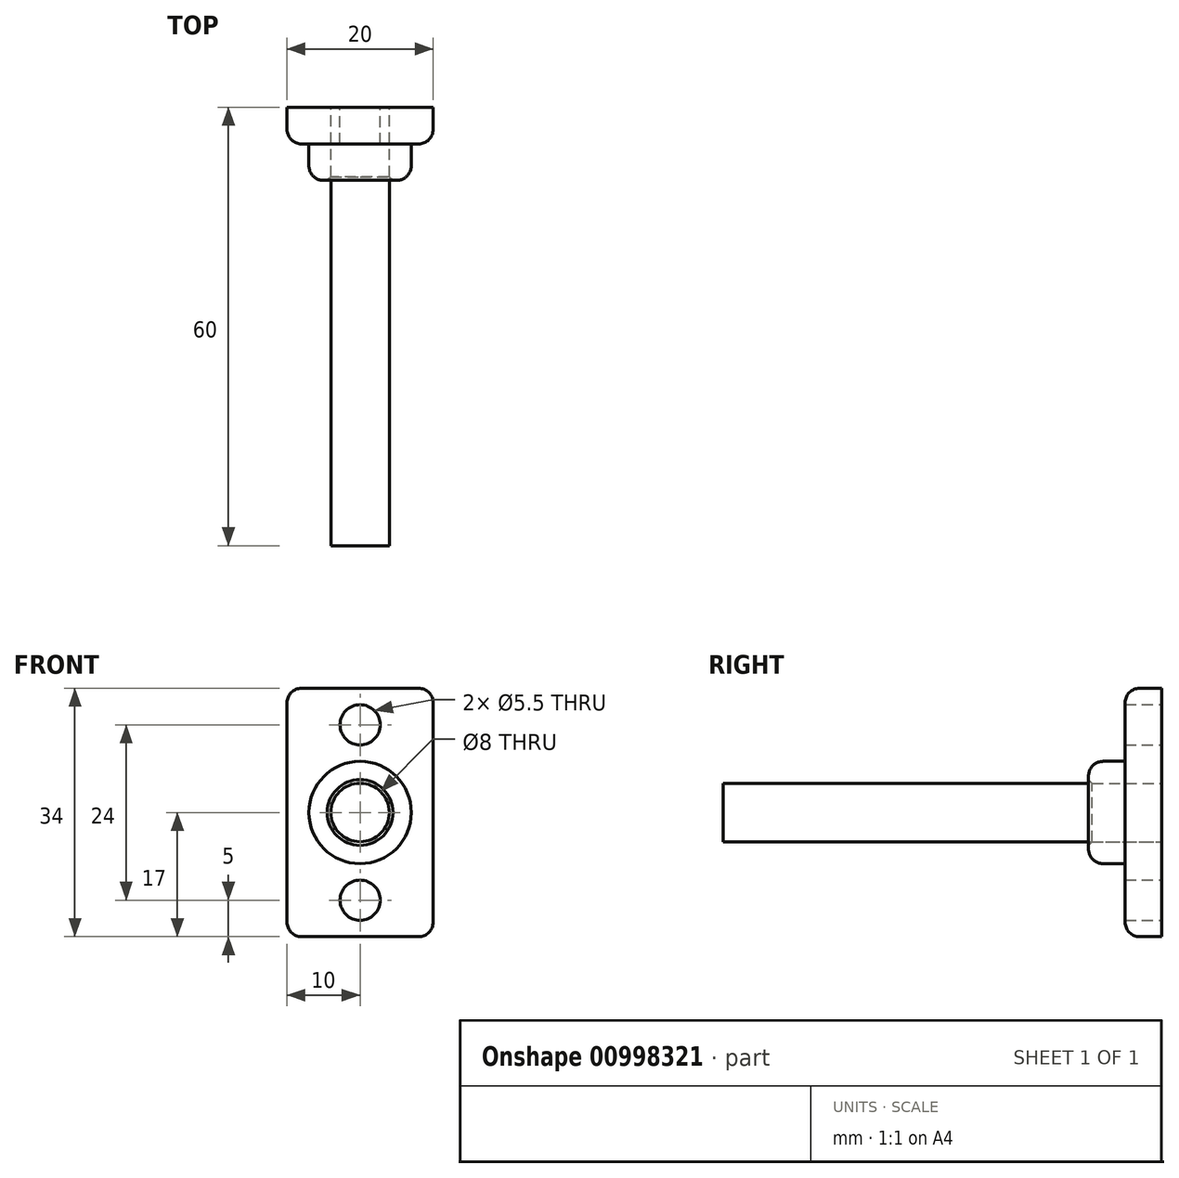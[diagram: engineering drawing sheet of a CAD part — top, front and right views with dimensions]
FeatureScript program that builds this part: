
annotation { "Feature Type Name" : "Feature", "Feature Type Description" : "" }
export const myFeature = defineFeature(function(context is Context, id is Id, definition is map)
    precondition{}
    {
        {
            var Q0;
            Q0=qCreatedBy(makeId("Front.planeOp"),FACE);
            var sketch = newSketch(context, id + "F0", { "sketchPlane" : qUnion([Q0])});
            skCircle(sketch, "E0", {"center": v(0, 0) * mm, "radius": 4 * mm});
            skCircle(sketch, "E1.0", {"center": v(0, 0) * mm, "radius": 7 * mm});
            skLineSegment(sketch, "E2.bottom", {"start": v(8, 17) * mm, "end": v(-8, 17) * mm});
            skLineSegment(sketch, "E2.top", {"start": v(8, -17) * mm, "end": v(-8, -17) * mm});
            skLineSegment(sketch, "E2.left", {"start": v(10, 15) * mm, "end": v(10, -15) * mm});
            skLineSegment(sketch, "E2.right", {"start": v(-10, 15) * mm, "end": v(-10, -15) * mm});
            skCircle(sketch, "E3", {"center": v(0, 12) * mm, "radius": 2.75 * mm});
            skCircle(sketch, "E4", {"center": v(0, -12) * mm, "radius": 2.75 * mm});
            skPoint(sketch, "E5.visualSharp", {"position": v(-10, 17) * mm});
            skArc(sketch, "E5.filletArc", {"start": v(-8, 17) * mm, "mid": v(-9.41, 16.41) * mm, "end": v(-10, 15) * mm});
            skPoint(sketch, "E6.visualSharp", {"position": v(10, 17) * mm});
            skArc(sketch, "E6.filletArc", {"start": v(10, 15) * mm, "mid": v(9.41, 16.41) * mm, "end": v(8, 17) * mm});
            skPoint(sketch, "E7.visualSharp", {"position": v(10, -17) * mm});
            skArc(sketch, "E7.filletArc", {"start": v(8, -17) * mm, "mid": v(9.41, -16.41) * mm, "end": v(10, -15) * mm});
            skPoint(sketch, "E8.visualSharp", {"position": v(-10, -17) * mm});
            skArc(sketch, "E8.filletArc", {"start": v(-10, -15) * mm, "mid": v(-9.41, -16.41) * mm, "end": v(-8, -17) * mm});
            skSolve(sketch);
        }
        {
            var Q0;
            Q0=makeQuery(id+"F0.imprint","IMPRINT",FACE,{"disambiguationData":[TD([[makeQuery(id+"F0.imprint","IMPRINT",EDGE,{"derivedFrom":sQuery(id+"F0.wireOp",EDGE,"E0")}),-1.0]])]});
            extrude(context, id + "F1", {"entities" : qUnion([Q0]), "depth" : 10 * mm, "offsetDistance" : 25 * mm});
        }
        {
            var Q0;
            Q0=makeQuery(id+"F0.imprint","IMPRINT",FACE,{"disambiguationData":[TD([[makeQuery(id+"F0.imprint","IMPRINT",EDGE,{"derivedFrom":sQuery(id+"F0.wireOp",EDGE,"E1.0")}),-1.0]])]});
            extrude(context, id + "F2", {"entities" : qUnion([Q0]), "operationType" : NewBodyOperationType.ADD, "depth" : 5 * mm, "offsetDistance" : 25 * mm});
        }
        {
            var Q0;
            Q0=makeQuery(id+"F0.imprint","IMPRINT",FACE,{"disambiguationData":[TD([[makeQuery(id+"F0.imprint","IMPRINT",EDGE,{"derivedFrom":sQuery(id+"F0.wireOp",EDGE,"E0")}),1.0]])]});
            extrude(context, id + "F3", {"entities" : qUnion([Q0]), "depth" : 60 * mm, "offsetDistance" : 25 * mm});
        }
        {
            var Q0;
            Q0=makeQuery(id+"F1.opExtrude","CAP_EDGE",EDGE,{"disambiguationData":[OSD([sQuery(id+"F0.wireOp",EDGE,"E1.0")])],"isStart":false});
            fillet(context, id + "F4", {"entities" : qUnion([Q0]), "radius" : 2 * mm, "tangentPropagation" : true, "allowEdgeOverflow" : false});
        }
        {
            var Q0;
            Q0=makeQuery(id+"F2.opExtrude","CAP_EDGE",EDGE,{"disambiguationData":[OSD([sQuery(id+"F0.wireOp",EDGE,"E2.left")])],"isStart":false});
            fillet(context, id + "F5", {"entities" : qUnion([Q0]), "radius" : 2 * mm, "tangentPropagation" : true, "allowEdgeOverflow" : false});
        }
        {
            var Q0;
            Q0=makeQuery(id+"F1.opExtrude","CAP_FACE",FACE,{"disambiguationData":[OSD([sQuery(id+"F0.wireOp",EDGE,"E0"),sQuery(id+"F0.wireOp",EDGE,"E1.0")])],"isStart":false});
            chamfer(context, id + "F6", {"entities" : qUnion([Q0]), "width" : 0.5 * mm, "tangentPropagation" : true});
        }
    });
